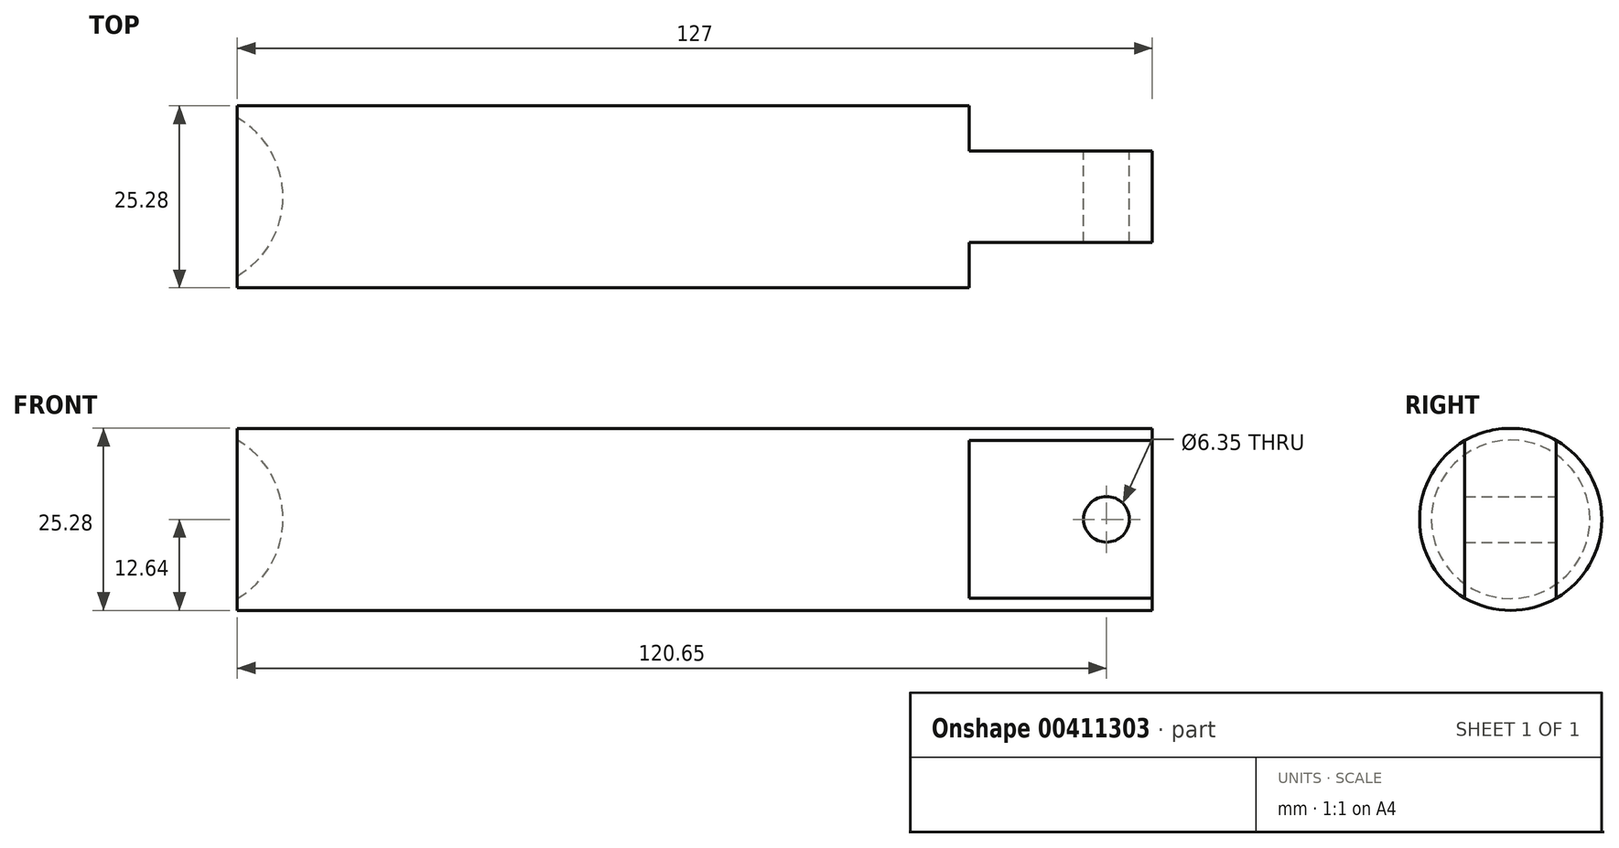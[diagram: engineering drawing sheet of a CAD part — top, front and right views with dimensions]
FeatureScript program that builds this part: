
annotation { "Feature Type Name" : "Feature", "Feature Type Description" : "" }
export const myFeature = defineFeature(function(context is Context, id is Id, definition is map)
    precondition{}
    {
        {
            var Q0;
            Q0=qCreatedBy(makeId("Front.planeOp"),FACE);
            var sketch = newSketch(context, id + "F0", { "sketchPlane" : qUnion([Q0])});
            skLineSegment(sketch, "E0", {"start": v(0, 0) * mm, "end": v(149.11, 0) * mm, "construction": true});
            skLineSegment(sketch, "E1.bottom", {"start": v(0, 0) * mm, "end": v(127, 0) * mm});
            skLineSegment(sketch, "E1.top", {"start": v(0, 12.64) * mm, "end": v(127, 12.64) * mm});
            skLineSegment(sketch, "E1.left", {"start": v(0, 0) * mm, "end": v(0, 12.64) * mm});
            skLineSegment(sketch, "E1.right", {"start": v(127, 0) * mm, "end": v(127, 12.64) * mm});
            skSolve(sketch);
        }
        {
            var Q0;
            Q0 = qSketchRegion(id + "F0", true);
            var Q1;
            Q1=sQuery(id+"F0.wireOp",EDGE,"E0");
            revolve(context, id + "F1", {"entities" : qUnion([Q0]), "axis" : qUnion([Q1]), "revolveType" : RevolveType.FULL});
        }
        {
            var Q0;
            Q0=qCreatedBy(makeId("Top.planeOp"),FACE);
            var sketch = newSketch(context, id + "F2", { "sketchPlane" : qUnion([Q0])});
            skLineSegment(sketch, "E2.0", {"start": v(127, -12.64) * mm, "end": v(127, -6.35) * mm});
            skLineSegment(sketch, "E3", {"start": v(101.6, 12.64) * mm, "end": v(127, 12.64) * mm});
            skLineSegment(sketch, "E4", {"start": v(127, -12.64) * mm, "end": v(101.6, -12.64) * mm});
            skLineSegment(sketch, "E5", {"start": v(0, 0) * mm, "end": v(169.5, 0) * mm, "construction": true});
            skLineSegment(sketch, "E6", {"start": v(101.6, 12.64) * mm, "end": v(101.6, 6.35) * mm});
            skLineSegment(sketch, "E7", {"start": v(101.6, 6.35) * mm, "end": v(127, 6.35) * mm});
            skLineSegment(sketch, "E8", {"start": v(127, -6.35) * mm, "end": v(101.6, -6.35) * mm});
            skLineSegment(sketch, "E9", {"start": v(101.6, -6.35) * mm, "end": v(101.6, -12.64) * mm});
            skLineSegment(sketch, "E10.trimOffspring", {"start": v(127, 6.35) * mm, "end": v(127, 12.64) * mm});
            skSolve(sketch);
        }
        {
            var Q0;
            Q0 = qSketchRegion(id + "F2", true);
            extrude(context, id + "F3", {"entities" : qUnion([Q0]), "operationType" : NewBodyOperationType.REMOVE, "endBound" : BoundingType.SYMMETRIC, "oppositeDirection" : true, "depth" : 25.4 * mm});
        }
        {
            var Q0;
            Q0=makeQuery(id+"F3.boolean.opBoolean","COPY",FACE,{"derivedFrom":makeQuery(id+"F3.opExtrude","SWEPT_FACE",FACE,{"disambiguationData":[OSD([sQuery(id+"F2.wireOp",EDGE,"E7")])]})});
            var sketch = newSketch(context, id + "F4", { "sketchPlane" : qUnion([Q0])});
            skLineSegment(sketch, "E11", {"start": v(0, 0) * mm, "end": v(-153.75, 0) * mm, "construction": true});
            skCircle(sketch, "E12", {"center": v(-120.65, 0) * mm, "radius": 3.18 * mm});
            skLineSegment(sketch, "E13.0", {"start": v(-127, -10.93) * mm, "end": v(-127, 10.93) * mm});
            skSolve(sketch);
        }
        {
            var Q0;
            Q0 = qSketchRegion(id + "F4", true);
            var Q1;
            Q1=makeQuery(id+"F3.boolean.opBoolean","COPY",FACE,{"derivedFrom":makeQuery(id+"F3.opExtrude","SWEPT_FACE",FACE,{"disambiguationData":[OSD([sQuery(id+"F2.wireOp",EDGE,"E8")])]})});
            extrude(context, id + "F5", {"entities" : qUnion([Q0]), "operationType" : NewBodyOperationType.REMOVE, "endBound" : BoundingType.UP_TO_SURFACE, "oppositeDirection" : true, "endBoundEntityFace" : qUnion([Q1]), "depth" : 25.4 * mm});
        }
        {
            var Q0;
            Q0=qCreatedBy(makeId("Front.planeOp"),FACE);
            var sketch = newSketch(context, id + "F6", { "sketchPlane" : qUnion([Q0])});
            skLineSegment(sketch, "E14", {"start": v(-6.35, -20.02) * mm, "end": v(-6.35, 16.18) * mm, "construction": true});
            skLineSegment(sketch, "E15", {"start": v(-12.8, 0) * mm, "end": v(9.22, 0) * mm, "construction": true});
            skArc(sketch, "E16", {"start": v(-6.35, -12.7) * mm, "mid": v(6.35, 0) * mm, "end": v(-6.35, 12.7) * mm});
            skLineSegment(sketch, "E17", {"start": v(-6.35, -12.7) * mm, "end": v(-6.35, 12.7) * mm});
            skSolve(sketch);
        }
        {
            var Q0;
            Q0 = qSketchRegion(id + "F6", true);
            var Q1;
            Q1=sQuery(id+"F6.wireOp",EDGE,"E14");
            revolve(context, id + "F7", {"operationType" : NewBodyOperationType.REMOVE, "entities" : qUnion([Q0]), "axis" : qUnion([Q1]), "revolveType" : RevolveType.FULL, "oppositeDirection" : true});
        }
    });
